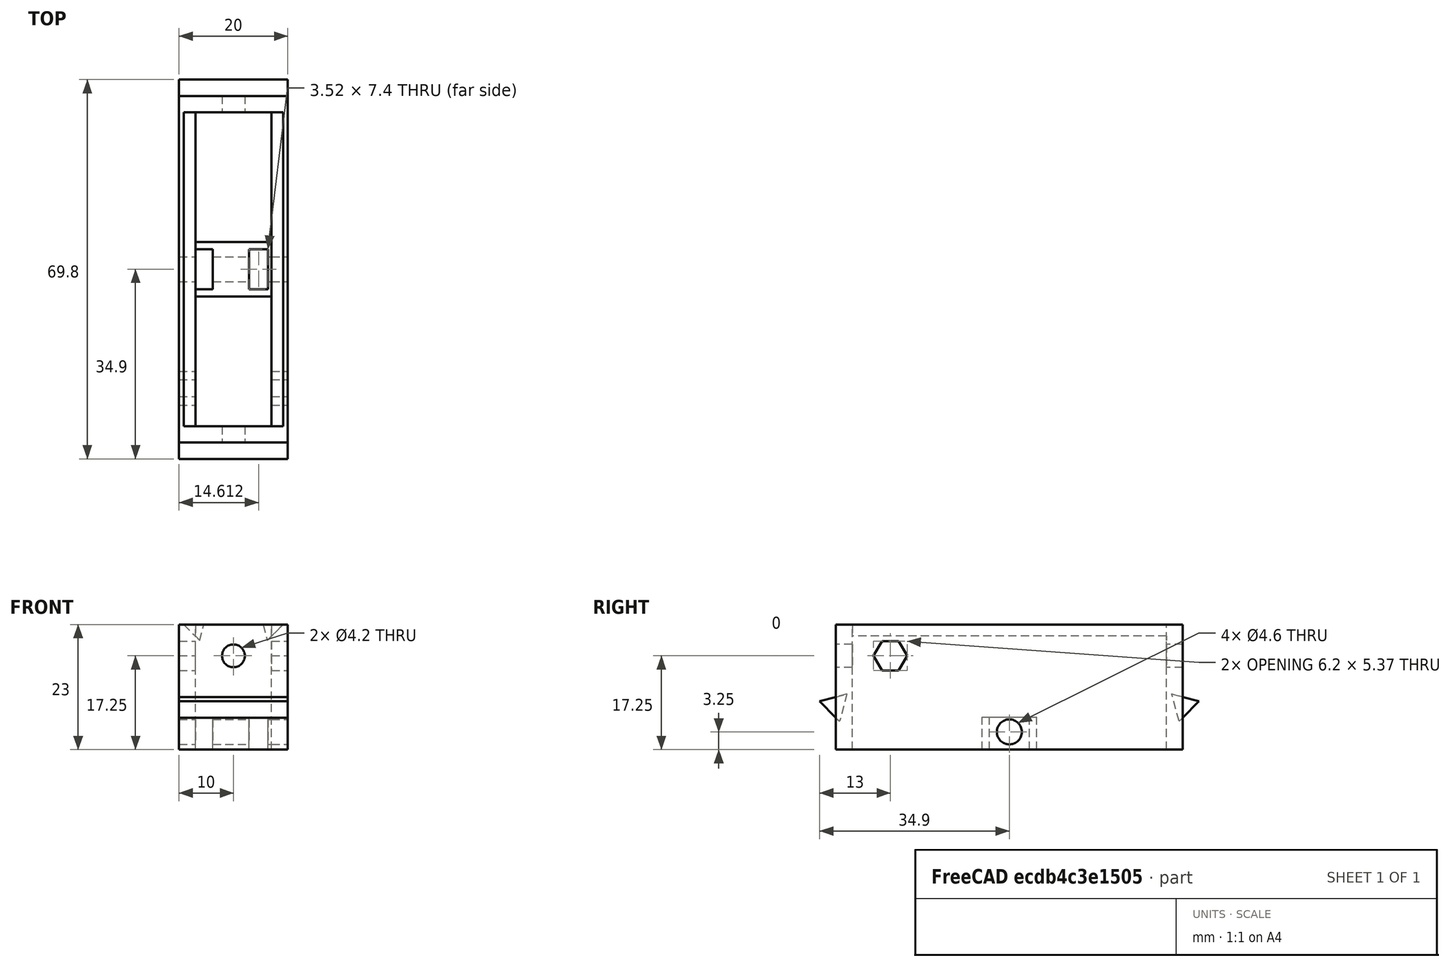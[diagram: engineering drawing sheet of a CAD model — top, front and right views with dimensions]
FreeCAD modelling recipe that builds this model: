
FCSTD DOCUMENT  (FreeCAD 0.19R23634 (Git))
Label: Stage-Bottom-Slider
License: All rights reserved
LicenseURL: http://en.wikipedia.org/wiki/All_rights_reserved
objects: Part::Prism×5, Part::Box×5, Part::MultiFuse×4, Part::Cylinder×3, Part::Cut×2, PartDesign::FeatureBase×2, PartDesign::Body×2, PartDesign::CoordinateSystem×2, App::Part×1
note: 25 computed .brp shape members not serialized (recipe doc carries the construction recipe); baked Part::Feature solids carry a one-line shape summary decoded from their .brp

FEATURE [Part::Cylinder] cylinder009
  Angle = 360
  AttacherType = Attacher::AttachEngine3D
  Height = 71
  Placement = pos=(-35.5,8e-15,11.75) rot=(0.57735,0.57735,0.57735;2.0944rad)
  Radius = 2.3
FEATURE [Part::Cylinder] cylinder007
  Angle = 360
  AttacherType = Attacher::AttachEngine3D
  Height = 71
  Placement = pos=(-35.5,8e-15,11.75) rot=(0.57735,0.57735,0.57735;2.0944rad)
  Radius = 2.3
FEATURE [Part::Prism] prism008
  AttacherType = Attacher::AttachEngine3D
  Circumradius = 3.1
  FirstAngle = 0
  Height = 21
  Placement = pos=(-10.5,-21.9,25.75) rot=(0.57735,0.57735,0.57735;2.0944rad)
  Polygon = 6
  SecondAngle = 0
FEATURE [Part::Box] cube012
  AttacherType = Attacher::AttachEngine3D
  Height = 6
  Length = 14
  Placement = pos=(-7,-5,8.5) rot=(0,0,1;0rad)
  Width = 10
FEATURE [Part::Prism] prism006
  AttacherType = Attacher::AttachEngine3D
  Circumradius = 3
  FirstAngle = 0
  Height = 57.8
  Placement = pos=(7,28.9,31.5) rot=(0.983106,-0.129428,0.129428;1.58783rad)
  Polygon = 3
  SecondAngle = 0
FEATURE [Part::Prism] prism007
  AttacherType = Attacher::AttachEngine3D
  Circumradius = 3
  FirstAngle = 0
  Height = 57.8
  Placement = pos=(-7,28.9,31.5) rot=(-0.092692,0.704063,-0.704063;3.32645rad)
  Polygon = 3
  SecondAngle = 0
FEATURE [Part::Prism] prism004
  AttacherType = Attacher::AttachEngine3D
  Circumradius = 3
  FirstAngle = 0
  Height = 20
  Placement = pos=(-10,32,16.6) rot=(0.621515,0.476905,0.621515;2.25159rad)
  Polygon = 3
  SecondAngle = 0
FEATURE [Part::Box] cube010
  AttacherType = Attacher::AttachEngine3D
  Height = 23
  Length = 20
  Placement = pos=(-10,-31.9,8.5) rot=(0,0,1;0rad)
  Width = 63.8
FEATURE [Part::Box] cube013
  AttacherType = Attacher::AttachEngine3D
  Height = 6
  Length = 3.2
  Placement = pos=(-7,-3.7,8.5) rot=(0,0,1;0rad)
  Width = 7.4
FEATURE [Part::Prism] prism005
  AttacherType = Attacher::AttachEngine3D
  Circumradius = 3
  FirstAngle = 0
  Height = 20
  Placement = pos=(-10,-32,16.6) rot=(0.621515,-0.476905,0.621515;4.0316rad)
  Polygon = 3
  SecondAngle = 0
FEATURE [Part::MultiFuse] Group003
  Shapes = -> [cube010,prism004,prism005]
FEATURE [Part::Box] cube014
  AttacherType = Attacher::AttachEngine3D
  Height = 6
  Length = 3.52
  Placement = pos=(2.85194,-3.7,8.5) rot=(0,0,1;0rad)
  Width = 7.4
FEATURE [Part::MultiFuse] Group005
  Shapes = -> [cylinder009,cube013,cube014]
FEATURE [Part::Cut] difference003
  Base = -> cube012
  Tool = -> Group005
FEATURE [PartDesign::FeatureBase] BaseFeature003
  BaseFeature = -> difference003
FEATURE [PartDesign::Body] Body003
  BaseFeature = -> difference003
  Group = -> [BaseFeature003]
  Origin = -> Origin003
  Tip = -> BaseFeature003
FEATURE [Part::Box] cube011
  AttacherType = Attacher::AttachEngine3D
  Height = 23
  Length = 14
  Placement = pos=(-7,-28.9,8.5) rot=(0,0,1;0rad)
  Width = 57.8
FEATURE [Part::Cylinder] cylinder008
  Angle = 360
  AttacherType = Attacher::AttachEngine3D
  Height = 71
  Placement = pos=(0,35.5,25.75) rot=(1,0,0;1.5708rad)
  Radius = 2.1
FEATURE [Part::MultiFuse] Group004
  Shapes = -> [cube011,cylinder007,cylinder008,prism006,prism007,prism008]
FEATURE [Part::Cut] difference002
  Base = -> Group003
  Tool = -> Group004
FEATURE [PartDesign::FeatureBase] BaseFeature002
  BaseFeature = -> difference002
FEATURE [PartDesign::Body] Body002
  BaseFeature = -> difference002
  Group = -> [BaseFeature002]
  Tip = -> BaseFeature002
FEATURE [Part::MultiFuse] Fusion  label="Bottom Slider"
  Shapes = -> [Body002,Body003]
FEATURE [PartDesign::CoordinateSystem] Slider
  AttacherType = Attacher::AttachEngine3D
  MapMode = 45
  Placement = pos=(-6.20099e-07,31.9,14.3787) rot=(0.57735,0.57735,0.57735;2.0944rad)
  Support = -> [Fusion]
FEATURE [PartDesign::CoordinateSystem] LCS_0001
  AttacherType = Attacher::AttachEngine3D
  MapMode = 45
  Placement = pos=(-1.4e-15,4.2e-15,8.5) rot=(0,0,1;0rad)
  Support = -> [Fusion]
FEATURE [App::Part] Bottom_Slider
  Group = -> [LCS_0001,prism007,Group003,cylinder008,cylinder007,Group005,difference003,prism006,cube010,cube013,cube011,cube012,Group004,prism004,difference002,prism008,cylinder009,Body003,prism005,Body002,cube014,Fusion,Slider]
  Origin = -> Origin002
